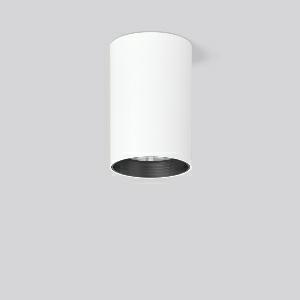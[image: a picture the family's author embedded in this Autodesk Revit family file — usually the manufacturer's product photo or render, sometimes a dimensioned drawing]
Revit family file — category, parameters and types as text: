
# Revit family: heledon_maxi_a_931228_002_3_76_5e7e
name_source: partatom
category: Lighting Fixtures
units: mm (PartAtom-declared; Revit-internal decimal feet)

## family parameters
Cut with Voids When Loaded = No
Host = Face
Light Source = No
Part Type = Normal
Room Calculation Point = No
Round Connector Dimension = Use Diameter
Shared = No

## types (1)
- HELEDON maxi A (1 x LED Modul 935, 3600 lm, 3500)
    Apparent Load = 35 VA
    Approval mark = CE
    CIE Flux Codes = 96 100 100 100 100
    Color Rendering = 92
    Color Temperature = 3500
    Default Elevation = 1800 mm
    Description = Series: HELEDON maxi
Cylindrical surface-mounted downlight. Housing: die-cast aluminium, powder-coated. Internal ceiling frame polycarbonate with bayonet mounting. Black plastic ring and recessed LED to prevent glare from the side. Optical assembly with lens made of plastic (polycarbonate) for the best homogeneous light distribution - can be changed without tools. Best colour rendering index Ra>90. Suitable for Ceiling mounting. Easy installation with a separate ceiling frame with bayonet mounting and plug connection. Driver integrated. Connected via plug-in connector. High quality converter without flickering and stroboscopic effect. The following accessories can be mounted without use of tools: interchangeable lenses, decorative glasses, honeycomb louvre, clear and frosted diffusers, white interchangeable plastic ring. 
Colour: traffic white, matt (RAL 9016)
Diameter: 123 mm
Height: 183 mm
Lamp: LED
Socket: without socket
Colour temperature: 3500K
Colour rendering index (CRI): 92
System power: 35 W
Rated luminous flux: 3600 lm
Luminous efficiency: 103 lm/W
Control gear: Converter, dimmable, DALI
Protection class: I
Type of protection: IP 20
    Height = 183 mm
    Lamp = 1 x LED Modul 935
    Lamp Light Flux = 3600 lm
    Lamp count = 1
    Length = 123 mm
    Lifetime = 50000 h
    Luminous efficacy = 103 lm/W
    Manufacturer = RZB
    ModVariant = No
    Model = 931228.002.3.76
    Mounting Place = Ceiling
    Mounting Type = Surface mounted
    Number of Poles = 1
    OnlyDefault = Yes
    Power Factor = 1
    Product Name = HELEDON maxi A
    Product group = Surface mounted downlights
    ProductGroupID = 302
    Protection Class = Protection class I
    Protection Degree = IP 20
    RLX_Detail_Level = 1
    RLX_Emergency_Light_Flux = 0 lm
    RLX_Emergency_Type = 0
    RLX_Emergency_Type_DB = No
    RlxData = <blob elided: 98129 chars, md5=df563f71>
    Socket = socket
    Standby Power = 0 W
    System Light Flux = 3600 lm
    System Power = 35 W
    Type Comments = Product without accessories
    Type Image = 931193.002.jpg
    URL = http://relux.com
    VarID = ---
    Voltage = 230 V
    Voltage Range = 220-240 V
    Weight = 0.00 kg
    Width = 0 mm  [stored 0 ft]

note: [stored X ft] marks values corroborated as IEEE doubles in the binary element streams (Revit-internal decimal feet)

## geometry (parser evidence)
native form markers: Blend x4, Sweep x9
no freeform markers — native parametric forms only
